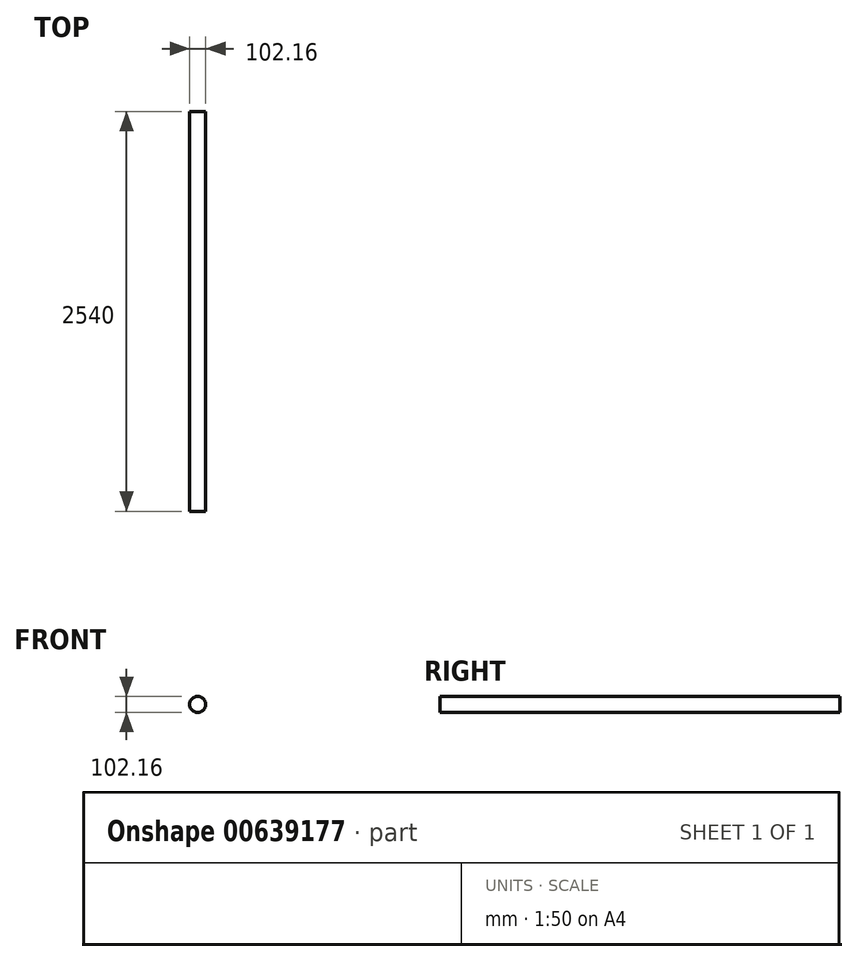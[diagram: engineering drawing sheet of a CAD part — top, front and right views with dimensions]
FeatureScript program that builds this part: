
annotation { "Feature Type Name" : "Feature", "Feature Type Description" : "" }
export const myFeature = defineFeature(function(context is Context, id is Id, definition is map)
    precondition{}
    {
        {
            var Q0;
            Q0=qCreatedBy(makeId("Front.planeOp"),FACE);
            var sketch = newSketch(context, id + "F0", { "sketchPlane" : qUnion([Q0])});
            skCircle(sketch, "E0", {"center": v(0, 0) * mm, "radius": 51.08 * mm});
            skSolve(sketch);
        }
        {
            var Q0;
            Q0=makeQuery(id+"F0.imprint","IMPRINT",FACE,{"disambiguationData":[TD([[makeQuery(id+"F0.imprint","IMPRINT",EDGE,{"derivedFrom":sQuery(id+"F0.wireOp",EDGE,"E0")}),1.0]])]});
            extrude(context, id + "F1", {"entities" : qUnion([Q0]), "depth" : 2540 * mm, "offsetDistance" : 25.4 * mm});
        }
    });
